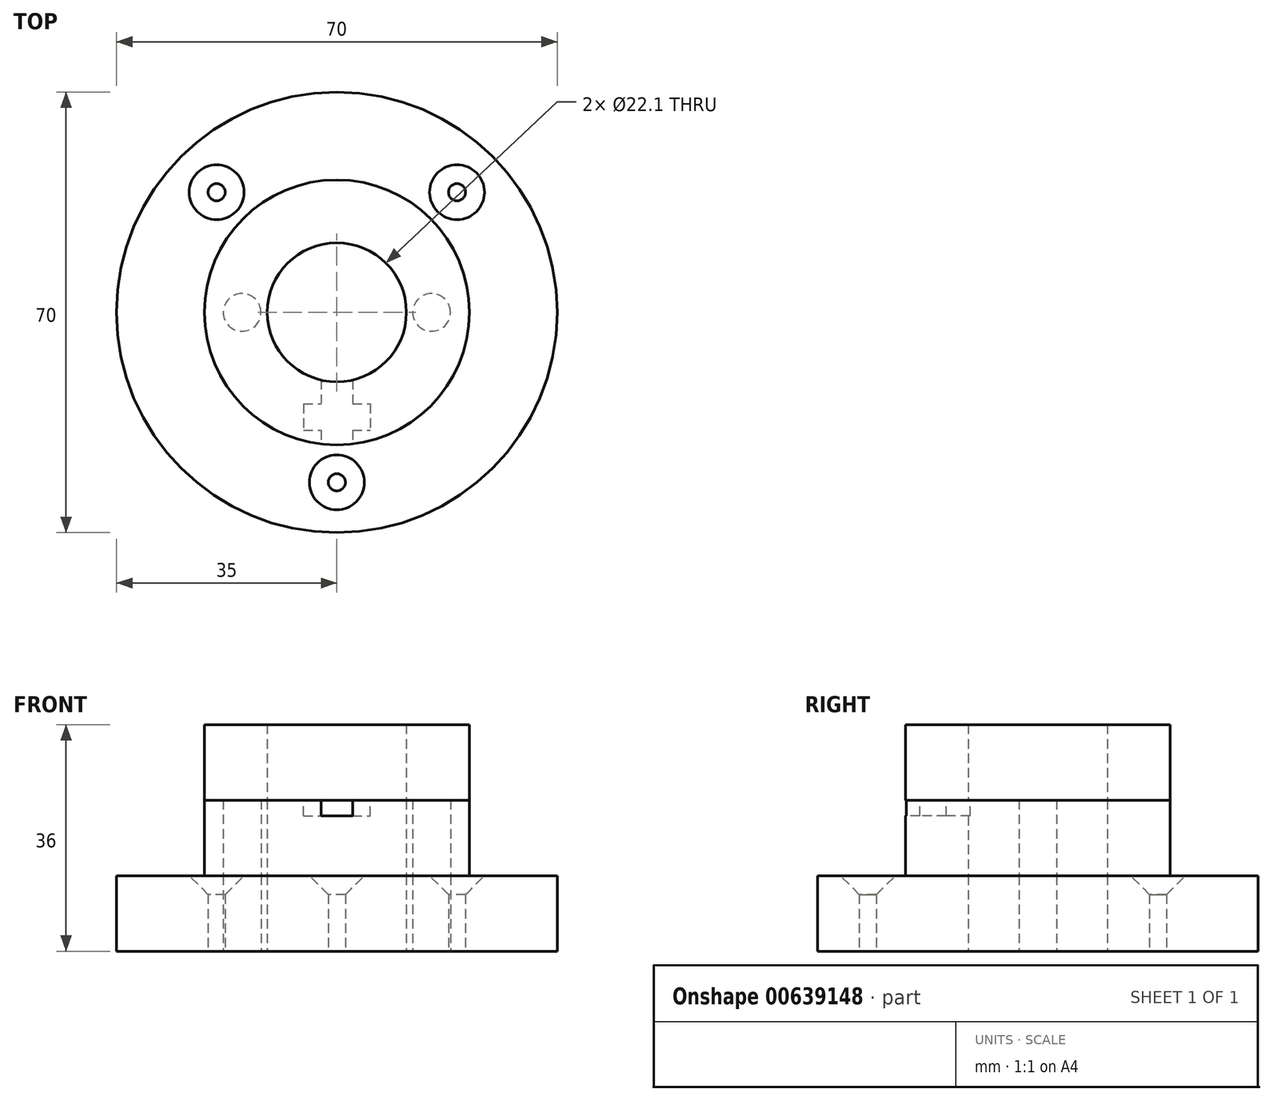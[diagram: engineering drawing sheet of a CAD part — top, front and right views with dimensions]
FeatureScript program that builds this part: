
annotation { "Feature Type Name" : "Feature", "Feature Type Description" : "" }
export const myFeature = defineFeature(function(context is Context, id is Id, definition is map)
    precondition{}
    {
        {
            var Q0;
            Q0=qCreatedBy(makeId("Top.planeOp"),FACE);
            var sketch = newSketch(context, id + "F0", { "sketchPlane" : qUnion([Q0])});
            skCircle(sketch, "E0", {"center": v(0, 0) * mm, "radius": 11.05 * mm});
            skCircle(sketch, "E1", {"center": v(0, 0) * mm, "radius": 35 * mm});
            skLineSegment(sketch, "E2", {"start": v(-35, 0) * mm, "end": v(35, 0) * mm, "construction": true});
            skLineSegment(sketch, "E3", {"start": v(0, 35) * mm, "end": v(0, -35) * mm, "construction": true});
            skCircle(sketch, "E4", {"center": v(-15.05, 0) * mm, "radius": 3 * mm});
            skCircle(sketch, "E5", {"center": v(15.05, 0) * mm, "radius": 3 * mm});
            skCircle(sketch, "E6", {"center": v(0, -27) * mm, "radius": 1.36 * mm});
            skCircle(sketch, "E7", {"center": v(19.1, 19.1) * mm, "radius": 1.36 * mm});
            skCircle(sketch, "E8", {"center": v(-19.1, 19.1) * mm, "radius": 1.36 * mm});
            skLineSegment(sketch, "E9", {"start": v(0, 0) * mm, "end": v(-24.75, 24.75) * mm, "construction": true});
            skLineSegment(sketch, "E10", {"start": v(0, 0) * mm, "end": v(24.75, 24.75) * mm, "construction": true});
            skSolve(sketch);
        }
        {
            var Q0;
            Q0=makeQuery(id+"F0.imprint","IMPRINT",FACE,{"disambiguationData":[TD([[makeQuery(id+"F0.imprint","IMPRINT",EDGE,{"derivedFrom":sQuery(id+"F0.wireOp",EDGE,"E0")}),-1.0]])]});
            extrude(context, id + "F1", {"entities" : qUnion([Q0]), "depth" : 12 * mm, "offsetDistance" : 25 * mm});
        }
        {
            var Q0;
            Q0=makeQuery(id+"F1.opExtrude","CAP_FACE",FACE,{"disambiguationData":[OSD([sQuery(id+"F0.wireOp",EDGE,"E0"),sQuery(id+"F0.wireOp",EDGE,"E1"),sQuery(id+"F0.wireOp",EDGE,"E4"),sQuery(id+"F0.wireOp",EDGE,"E5")])],"isStart":false});
            var sketch = newSketch(context, id + "F2", { "sketchPlane" : qUnion([Q0])});
            skCircle(sketch, "E11", {"center": v(0, 0) * mm, "radius": 21.05 * mm});
            skSolve(sketch);
        }
        {
            var Q0;
            Q0=makeQuery(id+"F2.imprint","IMPRINT",FACE,{"disambiguationData":[TD([[makeQuery(id+"F2.imprint","IMPRINT",EDGE,{"derivedFrom":sQuery(id+"F2.wireOp",EDGE,"E11")}),1.0]])]});
            extrude(context, id + "F3", {"entities" : qUnion([Q0]), "depth" : 12 * mm, "offsetDistance" : 25 * mm});
        }
        {
            var Q0;
            Q0=makeQuery(id+"F3.opExtrude","CAP_FACE",FACE,{"disambiguationData":[OSD([sQuery(id+"F0.wireOp",EDGE,"E0"),sQuery(id+"F0.wireOp",EDGE,"E4"),sQuery(id+"F0.wireOp",EDGE,"E5"),sQuery(id+"F2.wireOp",EDGE,"E11")])],"isStart":false});
            var sketch = newSketch(context, id + "F4", { "sketchPlane" : qUnion([Q0])});
            skLineSegment(sketch, "E12", {"start": v(0, 1.21) * mm, "end": v(0, -21.05) * mm, "construction": true});
            skLineSegment(sketch, "E13", {"start": v(-2.5, -10.76) * mm, "end": v(-2.5, -20.9) * mm});
            skLineSegment(sketch, "E14", {"start": v(2.5, -10.76) * mm, "end": v(2.5, -20.9) * mm});
            skLineSegment(sketch, "E15.bottom", {"start": v(-5.3, -14.54) * mm, "end": v(5.3, -14.54) * mm});
            skLineSegment(sketch, "E15.top", {"start": v(-5.3, -18.74) * mm, "end": v(5.3, -18.74) * mm});
            skLineSegment(sketch, "E15.left", {"start": v(-5.3, -14.54) * mm, "end": v(-5.3, -18.74) * mm});
            skLineSegment(sketch, "E15.right", {"start": v(5.3, -14.54) * mm, "end": v(5.3, -18.74) * mm});
            skSolve(sketch);
        }
        {
            var Q0;
            {var subQ0=sQuery(id+"F4.wireOp",EDGE,"E15.bottom");var subQ1=sQuery(id+"F4.wireOp",EDGE,"E13");var subQ2=makeQuery(id+"F4.imprint","INTERSECT",VERTEX,{"derivedFrom":[subQ1,subQ0]});Q0=makeQuery(id+"F4.imprint","IMPRINT",FACE,{"disambiguationData":[TD([[makeQuery(id+"F4.imprint","IMPRINT",EDGE,{"disambiguationData":[TD([[subQ2,-1.0]])],"derivedFrom":subQ1}),1.0]])]});}
            var Q1;
            {var subQ5=sQuery(id+"F4.wireOp",EDGE,"E15.left");Q1=makeQuery(id+"F4.imprint","IMPRINT",FACE,{"disambiguationData":[TD([[makeQuery(id+"F4.imprint","IMPRINT",EDGE,{"derivedFrom":subQ5}),1.0]])]});}
            var Q2;
            {var subQ0=sQuery(id+"F4.wireOp",EDGE,"E13");var subQ1=makeQuery(id+"F3.opExtrude","CAP_EDGE",EDGE,{"disambiguationData":[OSD([sQuery(id+"F0.wireOp",EDGE,"E0")])],"isStart":false});var subQ2=makeQuery(id+"F4.imprint","INTERSECT",VERTEX,{"derivedFrom":[subQ1,subQ0]});Q2=makeQuery(id+"F4.imprint","IMPRINT",FACE,{"disambiguationData":[TD([[makeQuery(id+"F4.imprint","IMPRINT",EDGE,{"disambiguationData":[TD([[subQ2,-1.0]])],"derivedFrom":subQ0}),1.0]])]});}
            var Q3;
            {var subQ5=sQuery(id+"F4.wireOp",EDGE,"E15.right");Q3=makeQuery(id+"F4.imprint","IMPRINT",FACE,{"disambiguationData":[TD([[makeQuery(id+"F4.imprint","IMPRINT",EDGE,{"derivedFrom":subQ5}),-1.0]])]});}
            var Q4;
            {var subQ0=sQuery(id+"F4.wireOp",EDGE,"E13");var subQ1=makeQuery(id+"F3.opExtrude","CAP_EDGE",EDGE,{"disambiguationData":[OSD([sQuery(id+"F2.wireOp",EDGE,"E11")])],"isStart":false});var subQ2=makeQuery(id+"F4.imprint","INTERSECT",VERTEX,{"derivedFrom":[subQ1,subQ0]});Q4=makeQuery(id+"F4.imprint","IMPRINT",FACE,{"disambiguationData":[TD([[makeQuery(id+"F4.imprint","IMPRINT",EDGE,{"disambiguationData":[TD([[subQ2,1.0]])],"derivedFrom":subQ0}),1.0]])]});}
            extrude(context, id + "F5", {"entities" : qUnion([Q0, Q1, Q2, Q3, Q4]), "operationType" : NewBodyOperationType.REMOVE, "oppositeDirection" : true, "depth" : 2.5 * mm, "offsetDistance" : 25 * mm});
        }
        {
            var Q0;
            Q0=makeQuery(id+"F3.opExtrude","CAP_FACE",FACE,{"disambiguationData":[OSD([sQuery(id+"F0.wireOp",EDGE,"E0"),sQuery(id+"F0.wireOp",EDGE,"E4"),sQuery(id+"F0.wireOp",EDGE,"E5"),sQuery(id+"F2.wireOp",EDGE,"E11")])],"isStart":false});
            var sketch = newSketch(context, id + "F6", { "sketchPlane" : qUnion([Q0])});
            skCircle(sketch, "E16", {"center": v(0, 0) * mm, "radius": 11.05 * mm});
            skCircle(sketch, "E17", {"center": v(0, 0) * mm, "radius": 21.05 * mm});
            skSolve(sketch);
        }
        {
            var Q0;
            Q0 = qSketchRegion(id + "F6", true);
            extrude(context, id + "F7", {"entities" : qUnion([Q0]), "depth" : 12 * mm, "offsetDistance" : 25 * mm});
        }
        {
            var Q0;
            Q0=makeQuery(id+"F1.opExtrude","CAP_EDGE",EDGE,{"disambiguationData":[OSD([sQuery(id+"F0.wireOp",EDGE,"E8")])],"isStart":false});
            var Q1;
            Q1=makeQuery(id+"F1.opExtrude","CAP_EDGE",EDGE,{"disambiguationData":[OSD([sQuery(id+"F0.wireOp",EDGE,"E6")])],"isStart":false});
            var Q2;
            Q2=makeQuery(id+"F1.opExtrude","CAP_EDGE",EDGE,{"disambiguationData":[OSD([sQuery(id+"F0.wireOp",EDGE,"E7")])],"isStart":false});
            chamfer(context, id + "F8", {"entities" : qUnion([Q0, Q1, Q2]), "width" : 3 * mm, "tangentPropagation" : true});
        }
    });
